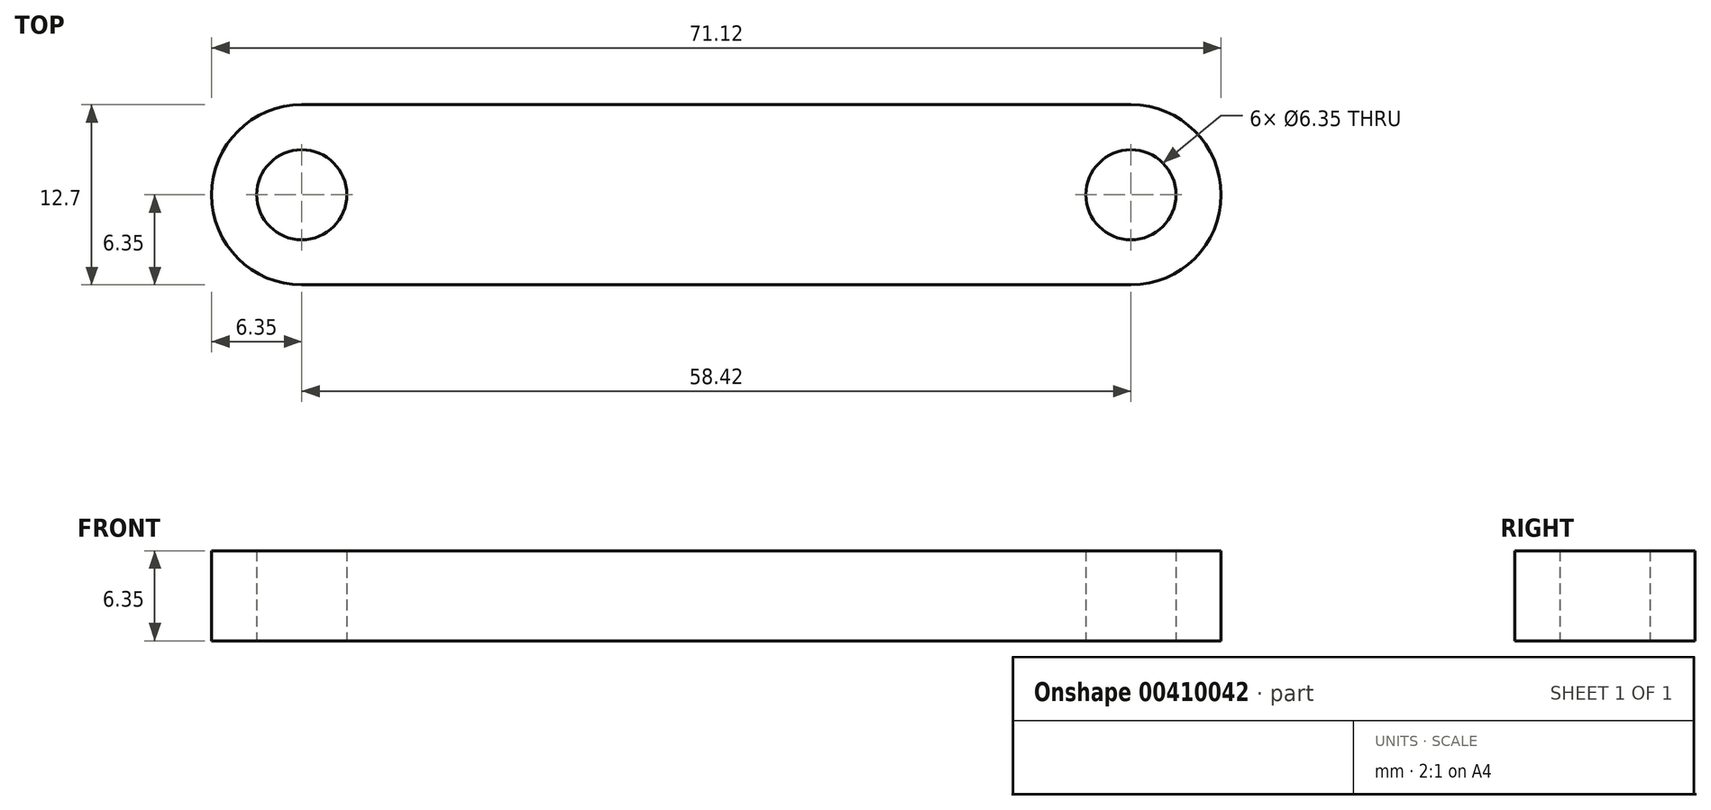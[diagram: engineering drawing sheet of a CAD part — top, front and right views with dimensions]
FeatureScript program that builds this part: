
annotation { "Feature Type Name" : "Feature", "Feature Type Description" : "" }
export const myFeature = defineFeature(function(context is Context, id is Id, definition is map)
    precondition{}
    {
        {
            var Q0;
            Q0=qCreatedBy(makeId("Top.planeOp"),FACE);
            var sketch = newSketch(context, id + "F0", { "sketchPlane" : qUnion([Q0])});
            skLineSegment(sketch, "E0", {"start": v(-29.21, 0) * mm, "end": v(29.21, 0) * mm, "construction": true});
            skLineSegment(sketch, "E1", {"start": v(0, 49.09) * mm, "end": v(0, -31.19) * mm, "construction": true});
            skArc(sketch, "E2.0.startCap", {"start": v(-29.21, -6.35) * mm, "mid": v(-35.56, 0) * mm, "end": v(-29.21, 6.35) * mm});
            skArc(sketch, "E2.0.endCap", {"start": v(29.21, 6.35) * mm, "mid": v(35.56, 0) * mm, "end": v(29.21, -6.35) * mm});
            skLineSegment(sketch, "E2.0.left", {"start": v(-29.21, 6.35) * mm, "end": v(29.21, 6.35) * mm});
            skLineSegment(sketch, "E2.0.right", {"start": v(-29.21, -6.35) * mm, "end": v(29.21, -6.35) * mm});
            skCircle(sketch, "E3", {"center": v(-29.21, 0) * mm, "radius": 3.18 * mm});
            skCircle(sketch, "E4.MirrorC", {"center": v(29.21, 0) * mm, "radius": 3.18 * mm});
            skSolve(sketch);
        }
        {
            var Q0;
            Q0 = qSketchRegion(id + "F0", true);
            extrude(context, id + "F1", {"entities" : qUnion([Q0]), "depth" : 6.35 * mm});
        }
    });
